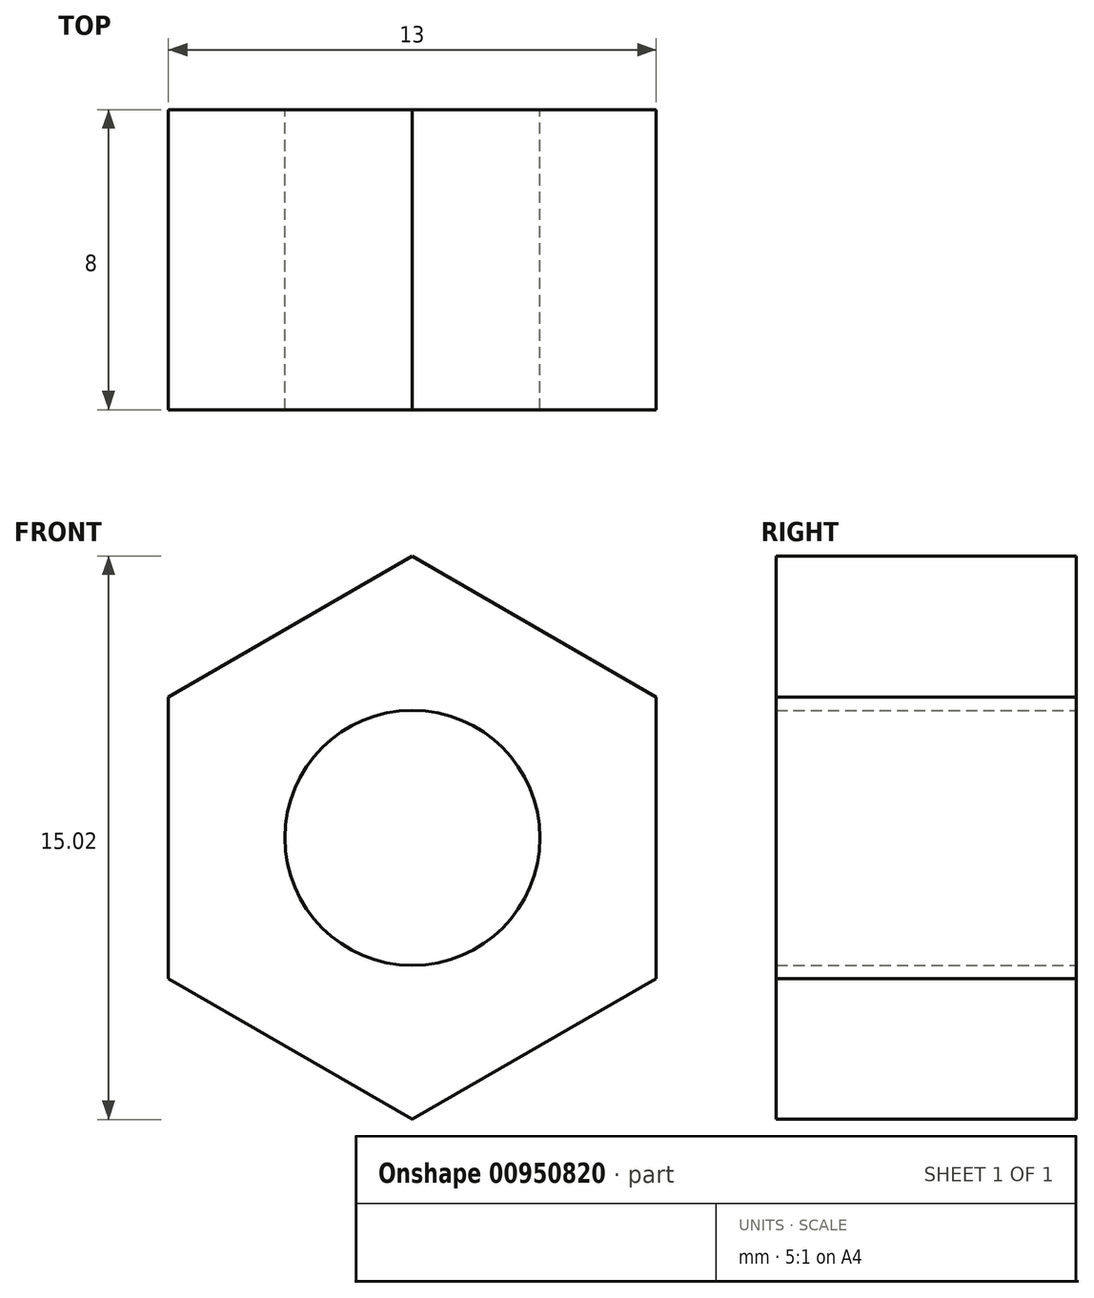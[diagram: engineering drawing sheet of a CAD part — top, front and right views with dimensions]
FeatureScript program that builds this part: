
annotation { "Feature Type Name" : "Feature", "Feature Type Description" : "" }
export const myFeature = defineFeature(function(context is Context, id is Id, definition is map)
    precondition{}
    {
        {
            var Q0;
            Q0=qCreatedBy(makeId("Front.planeOp"),FACE);
            var sketch = newSketch(context, id + "F0", { "sketchPlane" : qUnion([Q0])});
            skCircle(sketch, "E0.cCircle", {"center": v(0, 0) * mm, "radius": 6.5 * mm, "construction": true});
            skLineSegment(sketch, "E0.0", {"start": v(0, 7.5) * mm, "end": v(6.5, 3.75) * mm});
            skLineSegment(sketch, "E0.1", {"start": v(6.5, 3.75) * mm, "end": v(6.5, -3.75) * mm});
            skLineSegment(sketch, "E0.2", {"start": v(6.5, -3.75) * mm, "end": v(0, -7.5) * mm});
            skLineSegment(sketch, "E0.3", {"start": v(0, -7.5) * mm, "end": v(-6.5, -3.75) * mm});
            skLineSegment(sketch, "E0.4", {"start": v(-6.5, -3.75) * mm, "end": v(-6.5, 3.75) * mm});
            skLineSegment(sketch, "E0.5", {"start": v(-6.5, 3.75) * mm, "end": v(0, 7.5) * mm});
            skPoint(sketch, "E0.0.midPoint", {"position": v(3.25, 5.63) * mm});
            skCircle(sketch, "E1", {"center": v(0, 0) * mm, "radius": 3.4 * mm});
            skSolve(sketch);
        }
        {
            var Q0;
            Q0=qSketchRegion(id+"F0",true);
            extrude(context, id + "F1", {"entities" : qUnion([Q0]), "depth" : 8 * mm, "offsetDistance" : 25 * mm});
        }
    });
